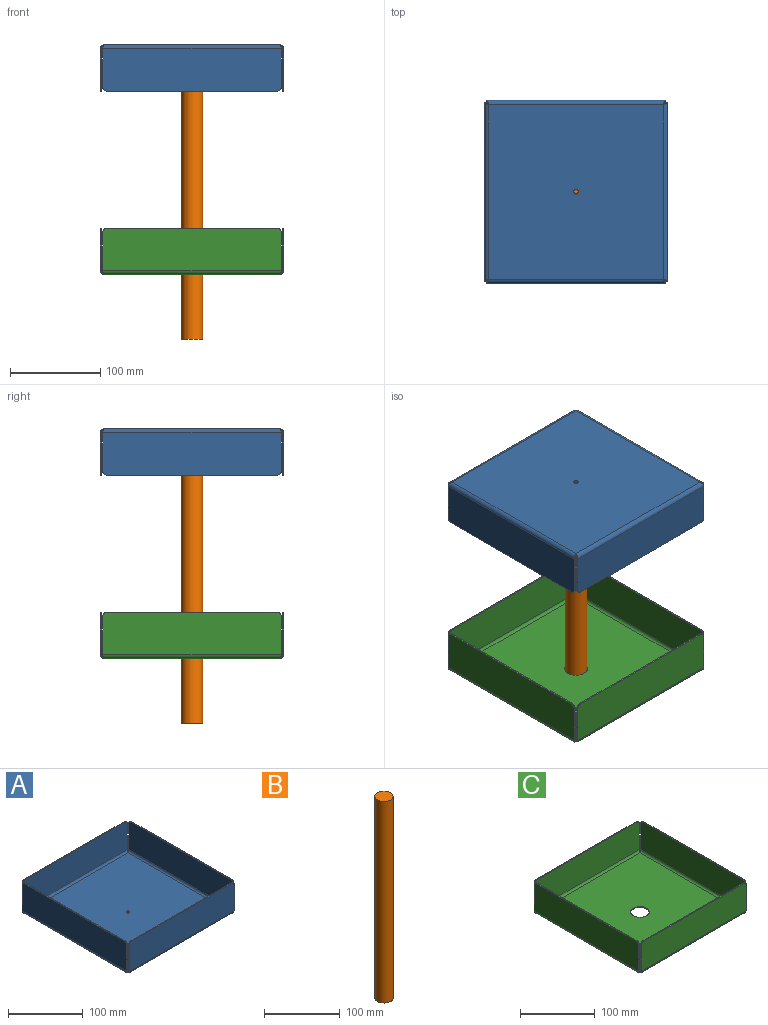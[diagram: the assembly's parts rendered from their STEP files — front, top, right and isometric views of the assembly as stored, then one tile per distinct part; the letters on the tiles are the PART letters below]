
ASSEMBLY  parts=3 mates=2
PART A: 51 faces, bbox 203x203x51.5 mm
  f0: plane 188x1.5mm, normal (0,0,1), area 282mm2, adj f3,f4,f5,f6
  f1: plane 42x1.5mm, normal (1,0,0), area 63mm2, adj f3,f4,f5,f47
  f2: plane 42x1.5mm, normal (-1,0,0), area 63mm2, adj f3,f4,f6,f48
  f3: plane 198x47mm, normal (0,1,0), area 9295.3mm2, adj f0,f1,f2,f5,f6,f49
  f4: plane 198x47mm, normal (0,-1,0), area 9295.3mm2, adj f0,f1,f2,f5,f6,f50
  f5: cylinder r=5mm len=5mm, axis (0,1,0), area 11.8mm2, adj f0,f1,f3,f4
  f6: cylinder r=5mm len=5mm, axis (0,-1,0), area 11.8mm2, adj f0,f2,f3,f4
  f7: cylinder r=2.5mm len=5mm, axis (0,0,1), area 23.6mm2, adj f8,f9
  f8: plane 194x194mm, normal (0,0,-1), area 37615.4mm2, adj f7,f10,f11,f12,f13,f23,f34,f45
  f9: plane 194x194mm, normal (0,0,1), area 37615.4mm2, adj f7,f10,f11,f12,f13,f24,f35,f46
  f10: plane 1.5x0.71mm, normal (0.71,0.71,0), area 1.5mm2, adj f8,f9,f44,f47
  f11: plane 1.5x0.71mm, normal (0.71,-0.71,0), area 1.5mm2, adj f8,f9,f21,f43
  f12: plane 1.5x0.71mm, normal (-0.71,-0.71,0), area 1.5mm2, adj f8,f9,f22,f32
  f13: plane 1.5x0.71mm, normal (-0.71,0.71,0), area 1.5mm2, adj f8,f9,f33,f48
  f14: plane 188x1.5mm, normal (0,0,1), area 282mm2, adj f17,f18,f19,f20
  f15: plane 42x1.5mm, normal (-1,0,0), area 63mm2, adj f17,f18,f19,f22
  f16: plane 42x1.5mm, normal (1,0,0), area 63mm2, adj f17,f18,f20,f21
  f17: plane 198x47mm, normal (0,-1,0), area 9295.3mm2, adj f14,f15,f16,f19,f20,f23
  f18: plane 198x47mm, normal (0,1,0), area 9295.3mm2, adj f14,f15,f16,f19,f20,f24
  f19: cylinder r=5mm len=5mm, axis (0,1,0), area 11.8mm2, adj f14,f15,f17,f18
  f20: cylinder r=5mm len=5mm, axis (0,-1,0), area 11.8mm2, adj f14,f16,f17,f18
  f21: bspline ~4.5x4.5mm, area 9.9mm2, adj f11,f16,f23,f24
  f22: bspline ~4.5x4.5mm, area 9.9mm2, adj f12,f15,f23,f24
  f23: cylinder r=4.5mm len=198mm, axis (1,0,0), area 1386.1mm2, adj f8,f17,f21,f22
  f24: cylinder r=3mm len=198mm, axis (1,0,0), area 924.1mm2, adj f9,f18,f21,f22
  f25: plane 188x1.5mm, normal (0,0,1), area 282mm2, adj f28,f29,f30,f31
  f26: plane 42x1.5mm, normal (0,1,0), area 63mm2, adj f28,f29,f30,f33
  f27: plane 42x1.5mm, normal (0,-1,0), area 63mm2, adj f28,f29,f31,f32
  f28: plane 198x47mm, normal (-1,0,0), area 9295.3mm2, adj f25,f26,f27,f30,f31,f34
  f29: plane 198x47mm, normal (1,0,0), area 9295.3mm2, adj f25,f26,f27,f30,f31,f35
  f30: cylinder r=5mm len=5mm, axis (1,0,0), area 11.8mm2, adj f25,f26,f28,f29
  f31: cylinder r=5mm len=5mm, axis (-1,0,0), area 11.8mm2, adj f25,f27,f28,f29
  f32: bspline ~4.5x4.5mm, area 9.9mm2, adj f12,f27,f34,f35
  f33: bspline ~4.5x4.5mm, area 9.9mm2, adj f13,f26,f34,f35
  f34: cylinder r=4.5mm len=198mm, axis (0,-1,0), area 1386.1mm2, adj f8,f28,f32,f33
  f35: cylinder r=3mm len=198mm, axis (0,-1,0), area 924.1mm2, adj f9,f29,f32,f33
  f36: plane 188x1.5mm, normal (0,0,1), area 282mm2, adj f39,f40,f41,f42
  f37: plane 42x1.5mm, normal (0,-1,0), area 63mm2, adj f39,f40,f42,f43
  f38: plane 42x1.5mm, normal (0,1,0), area 63mm2, adj f39,f40,f41,f44
  f39: plane 198x47mm, normal (1,0,0), area 9295.3mm2, adj f36,f37,f38,f41,f42,f45
  f40: plane 198x47mm, normal (-1,0,0), area 9295.3mm2, adj f36,f37,f38,f41,f42,f46
  f41: cylinder r=5mm len=5mm, axis (-1,0,0), area 11.8mm2, adj f36,f38,f39,f40
  f42: cylinder r=5mm len=5mm, axis (1,0,0), area 11.8mm2, adj f36,f37,f39,f40
  f43: bspline ~4.5x4.5mm, area 9.9mm2, adj f11,f37,f45,f46
  f44: bspline ~4.5x4.5mm, area 9.9mm2, adj f10,f38,f45,f46
  f45: cylinder r=4.5mm len=198mm, axis (0,-1,0), area 1386.1mm2, adj f8,f39,f43,f44
  f46: cylinder r=3mm len=198mm, axis (0,-1,0), area 924mm2, adj f9,f40,f43,f44
  f47: bspline ~4.5x4.5mm, area 9.9mm2, adj f1,f10,f49,f50
  f48: bspline ~4.5x4.5mm, area 9.9mm2, adj f2,f13,f49,f50
  f49: cylinder r=4.5mm len=198mm, axis (1,0,0), area 1386.1mm2, adj f3,f8,f47,f48
  f50: cylinder r=3mm len=198mm, axis (1,0,0), area 924mm2, adj f4,f9,f47,f48
PART B: 3 faces, bbox 24x24x325 mm
  f0: cylinder r=12mm len=325mm, axis (0,0,-1), area 24504.4mm2, adj f1,f2
  f1: plane 24x24mm, normal (0,0,1), area 452.4mm2, adj f0
  f2: plane 24x24mm, normal (0,0,-1), area 452.4mm2, adj f0
PART C: 51 faces, bbox 203x203x51.5 mm
  f0: plane 188x1.5mm, normal (0,0,1), area 282mm2, adj f3,f4,f5,f6
  f1: plane 42x1.5mm, normal (1,0,0), area 63mm2, adj f3,f4,f5,f47
  f2: plane 42x1.5mm, normal (-1,0,0), area 63mm2, adj f3,f4,f6,f48
  f3: plane 198x47mm, normal (0,1,0), area 9295.3mm2, adj f0,f1,f2,f5,f6,f49
  f4: plane 198x47mm, normal (0,-1,0), area 9295.3mm2, adj f0,f1,f2,f5,f6,f50
  f5: cylinder r=5mm len=5mm, axis (0,1,0), area 11.8mm2, adj f0,f1,f3,f4
  f6: cylinder r=5mm len=5mm, axis (0,-1,0), area 11.8mm2, adj f0,f2,f3,f4
  f7: cylinder r=12.5mm len=25mm, axis (0,0,1), area 117.8mm2, adj f8,f9
  f8: plane 194x194mm, normal (0,0,-1), area 37144.1mm2, adj f7,f10,f11,f12,f13,f23,f34,f45
  f9: plane 194x194mm, normal (0,0,1), area 37144.1mm2, adj f7,f10,f11,f12,f13,f24,f35,f46
  f10: plane 1.5x0.71mm, normal (0.71,0.71,0), area 1.5mm2, adj f8,f9,f44,f47
  f11: plane 1.5x0.71mm, normal (0.71,-0.71,0), area 1.5mm2, adj f8,f9,f21,f43
  f12: plane 1.5x0.71mm, normal (-0.71,-0.71,0), area 1.5mm2, adj f8,f9,f22,f32
  f13: plane 1.5x0.71mm, normal (-0.71,0.71,0), area 1.5mm2, adj f8,f9,f33,f48
  f14: plane 188x1.5mm, normal (0,0,1), area 282mm2, adj f17,f18,f19,f20
  f15: plane 42x1.5mm, normal (-1,0,0), area 63mm2, adj f17,f18,f19,f22
  f16: plane 42x1.5mm, normal (1,0,0), area 63mm2, adj f17,f18,f20,f21
  f17: plane 198x47mm, normal (0,-1,0), area 9295.3mm2, adj f14,f15,f16,f19,f20,f23
  f18: plane 198x47mm, normal (0,1,0), area 9295.3mm2, adj f14,f15,f16,f19,f20,f24
  f19: cylinder r=5mm len=5mm, axis (0,1,0), area 11.8mm2, adj f14,f15,f17,f18
  f20: cylinder r=5mm len=5mm, axis (0,-1,0), area 11.8mm2, adj f14,f16,f17,f18
  f21: bspline ~4.5x4.5mm, area 9.9mm2, adj f11,f16,f23,f24
  f22: bspline ~4.5x4.5mm, area 9.9mm2, adj f12,f15,f23,f24
  f23: cylinder r=4.5mm len=198mm, axis (1,0,0), area 1386.1mm2, adj f8,f17,f21,f22
  f24: cylinder r=3mm len=198mm, axis (1,0,0), area 924.1mm2, adj f9,f18,f21,f22
  f25: plane 188x1.5mm, normal (0,0,1), area 282mm2, adj f28,f29,f30,f31
  f26: plane 42x1.5mm, normal (0,1,0), area 63mm2, adj f28,f29,f30,f33
  f27: plane 42x1.5mm, normal (0,-1,0), area 63mm2, adj f28,f29,f31,f32
  f28: plane 198x47mm, normal (-1,0,0), area 9295.3mm2, adj f25,f26,f27,f30,f31,f34
  f29: plane 198x47mm, normal (1,0,0), area 9295.3mm2, adj f25,f26,f27,f30,f31,f35
  f30: cylinder r=5mm len=5mm, axis (1,0,0), area 11.8mm2, adj f25,f26,f28,f29
  f31: cylinder r=5mm len=5mm, axis (-1,0,0), area 11.8mm2, adj f25,f27,f28,f29
  f32: bspline ~4.5x4.5mm, area 9.9mm2, adj f12,f27,f34,f35
  f33: bspline ~4.5x4.5mm, area 9.9mm2, adj f13,f26,f34,f35
  f34: cylinder r=4.5mm len=198mm, axis (0,-1,0), area 1386.1mm2, adj f8,f28,f32,f33
  f35: cylinder r=3mm len=198mm, axis (0,-1,0), area 924.1mm2, adj f9,f29,f32,f33
  f36: plane 188x1.5mm, normal (0,0,1), area 282mm2, adj f39,f40,f41,f42
  f37: plane 42x1.5mm, normal (0,-1,0), area 63mm2, adj f39,f40,f42,f43
  f38: plane 42x1.5mm, normal (0,1,0), area 63mm2, adj f39,f40,f41,f44
  f39: plane 198x47mm, normal (1,0,0), area 9295.3mm2, adj f36,f37,f38,f41,f42,f45
  f40: plane 198x47mm, normal (-1,0,0), area 9295.3mm2, adj f36,f37,f38,f41,f42,f46
  f41: cylinder r=5mm len=5mm, axis (-1,0,0), area 11.8mm2, adj f36,f38,f39,f40
  f42: cylinder r=5mm len=5mm, axis (1,0,0), area 11.8mm2, adj f36,f37,f39,f40
  f43: bspline ~4.5x4.5mm, area 9.9mm2, adj f11,f37,f45,f46
  f44: bspline ~4.5x4.5mm, area 9.9mm2, adj f10,f38,f45,f46
  f45: cylinder r=4.5mm len=198mm, axis (0,-1,0), area 1386.1mm2, adj f8,f39,f43,f44
  f46: cylinder r=3mm len=198mm, axis (0,-1,0), area 924mm2, adj f9,f40,f43,f44
  f47: bspline ~4.5x4.5mm, area 9.9mm2, adj f1,f10,f49,f50
  f48: bspline ~4.5x4.5mm, area 9.9mm2, adj f2,f13,f49,f50
  f49: cylinder r=4.5mm len=198mm, axis (1,0,0), area 1386.1mm2, adj f3,f8,f47,f48
  f50: cylinder r=3mm len=198mm, axis (1,0,0), area 924mm2, adj f4,f9,f47,f48
PLACE A rot(axis=(0,1,0),180deg) t=(35.62,117.49,171.39)mm
PLACE B t=(-164.38,117.49,-128.61)mm
PLACE C t=(-164.38,117.49,-80.48)mm
MATE slider B.f0 <-> C.f7  axis (0,0,-1) through (-64.38,17.49,-153.61)mm
MATE fastened A.f7 <-> B.f0  axis (0,0,-1) through (-64.38,17.49,171.39)mm
